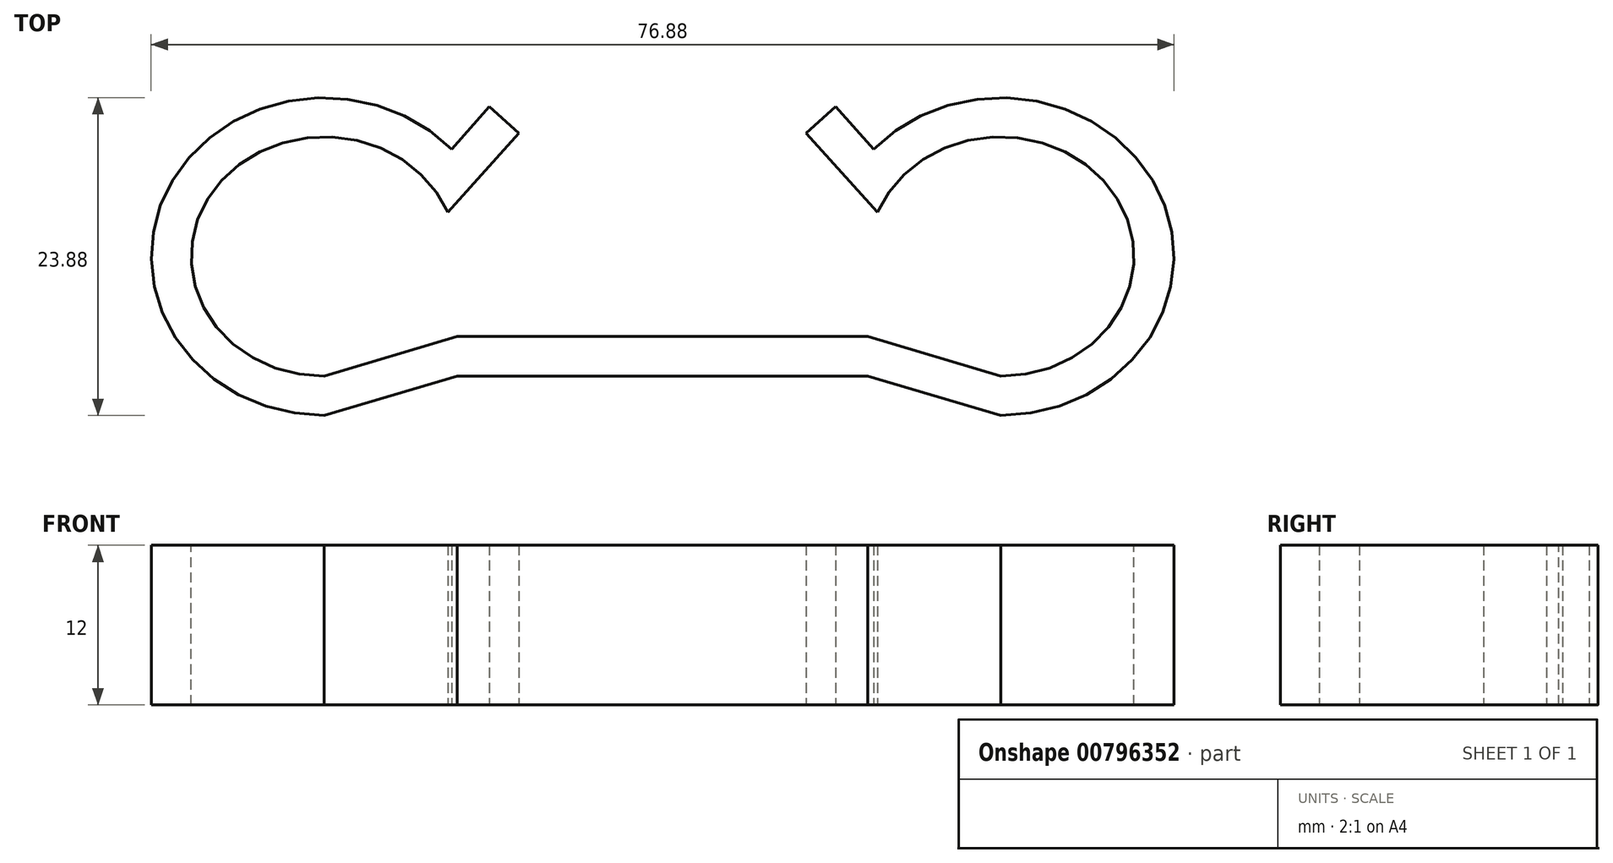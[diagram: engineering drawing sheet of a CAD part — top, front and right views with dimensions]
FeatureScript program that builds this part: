
annotation { "Feature Type Name" : "Feature", "Feature Type Description" : "" }
export const myFeature = defineFeature(function(context is Context, id is Id, definition is map)
    precondition{}
    {
        {
            var Q0;
            Q0=qCreatedBy(makeId("Top.planeOp"),FACE);
            var sketch = newSketch(context, id + "F0", { "sketchPlane" : qUnion([Q0])});
            skLineSegment(sketch, "E0.MirrorCS", {"start": v(0, 0) * mm, "end": v(15.44, 0) * mm});
            skLineSegment(sketch, "E1", {"start": v(-25.44, 0) * mm, "end": v(-25.44, 9) * mm, "construction": true});
            skLineSegment(sketch, "E2", {"start": v(-25.44, 9) * mm, "end": v(-35.44, 9) * mm, "construction": true});
            skLineSegment(sketch, "E3.MirrorCS", {"start": v(-25.44, 9) * mm, "end": v(-15.44, 9) * mm, "construction": true});
            skLineSegment(sketch, "E4.MirrorCS", {"start": v(-25.44, 18) * mm, "end": v(-25.44, 9) * mm, "construction": true});
            skEllipticalArc(sketch, "E5", {});
            skLineSegment(sketch, "E6", {"start": v(-15.44, 9) * mm, "end": v(-15.44, 3) * mm, "construction": true});
            skLineSegment(sketch, "E7", {"start": v(-15.44, 9) * mm, "end": v(-16.15, 12.33) * mm, "construction": true});
            skLineSegment(sketch, "E8", {"start": v(-16.15, 12.33) * mm, "end": v(-4.43, 12.33) * mm, "construction": true});
            skLineSegment(sketch, "E9", {"start": v(-16.15, 12.33) * mm, "end": v(-16.15, 23.8) * mm, "construction": true});
            skLineSegment(sketch, "E10", {"start": v(-16.15, 12.33) * mm, "end": v(-14.01, 14.7) * mm});
            skLineSegment(sketch, "E11", {"start": v(0, 0) * mm, "end": v(0, -2.94) * mm, "construction": true});
            skLineSegment(sketch, "E12", {"start": v(25.44, 0) * mm, "end": v(25.44, -2.94) * mm, "construction": true});
            skLineSegment(sketch, "E13.MirrorCS", {"start": v(-25.44, 0) * mm, "end": v(-25.44, -2.94) * mm, "construction": true});
            skLineSegment(sketch, "E14", {"start": v(-25.44, 18) * mm, "end": v(-25.44, 21) * mm, "construction": true});
            skPoint(sketch, "E15.MirrorCS.end.orphan", {"position": v(10.8, 18.28) * mm});
            skPoint(sketch, "E15.MirrorCS.start.orphan", {"position": v(16.15, 12.33) * mm});
            skPoint(sketch, "E16.MirrorCS.start.orphan", {"position": v(25.44, 0) * mm});
            skLineSegment(sketch, "E17", {"start": v(-35.44, 9) * mm, "end": v(-38.44, 9) * mm, "construction": true});
            skEllipticalArc(sketch, "E18", {});
            skLineSegment(sketch, "E19", {"start": v(-14.01, 14.7) * mm, "end": v(-15.86, 17.07) * mm, "construction": true});
            skLineSegment(sketch, "E20", {"start": v(-25.44, 18) * mm, "end": v(-15.86, 18) * mm, "construction": true});
            skLineSegment(sketch, "E21", {"start": v(-10.8, 18.28) * mm, "end": v(-13.03, 20.28) * mm});
            skLineSegment(sketch, "E22", {"start": v(-15.86, 17.07) * mm, "end": v(-13.03, 20.28) * mm});
            skEllipticalArc(sketch, "E23.MirrorCS", {});
            skEllipticalArc(sketch, "E24.MirrorCS", {});
            skPoint(sketch, "E25.MirrorCS.end.orphan", {"position": v(13.03, 20.28) * mm});
            skPoint(sketch, "E25.MirrorCS.start.orphan", {"position": v(15.86, 17.07) * mm});
            skLineSegment(sketch, "E26", {"start": v(-16.15, 12.33) * mm, "end": v(-10.8, 18.28) * mm});
            skLineSegment(sketch, "E27.MirrorCS", {"start": v(16.15, 12.33) * mm, "end": v(10.8, 18.28) * mm});
            skLineSegment(sketch, "E28.MirrorCS", {"start": v(10.8, 18.28) * mm, "end": v(13.03, 20.28) * mm});
            skLineSegment(sketch, "E29.MirrorCS", {"start": v(15.86, 17.07) * mm, "end": v(13.03, 20.28) * mm});
            skLineSegment(sketch, "E30", {"start": v(-15.44, 0) * mm, "end": v(-15.44, 3) * mm, "construction": true});
            skLineSegment(sketch, "E31", {"start": v(-25.44, 0) * mm, "end": v(-25.44, 3) * mm});
            skLineSegment(sketch, "E32", {"start": v(-25.44, 3) * mm, "end": v(-15.44, 3) * mm, "construction": true});
            skLineSegment(sketch, "E33", {"start": v(-25.44, 0) * mm, "end": v(-15.44, 3) * mm});
            skLineSegment(sketch, "E34", {"start": v(-25.44, -2.94) * mm, "end": v(-15.44, 0) * mm});
            skLineSegment(sketch, "E35", {"start": v(-15.44, 3) * mm, "end": v(0, 3) * mm});
            skLineSegment(sketch, "E36", {"start": v(-15.44, 0) * mm, "end": v(0, 0) * mm});
            skLineSegment(sketch, "E37.MirrorCS", {"start": v(25.44, 0) * mm, "end": v(15.44, 3) * mm});
            skLineSegment(sketch, "E38.MirrorCS", {"start": v(25.44, -2.94) * mm, "end": v(15.44, 0) * mm});
            skLineSegment(sketch, "E39.MirrorCS", {"start": v(15.44, 0) * mm, "end": v(15.44, 3) * mm, "construction": true});
            skLineSegment(sketch, "E40.MirrorCS", {"start": v(15.44, 3) * mm, "end": v(0, 3) * mm});
            const initialGuessF0  = {"E5": [-0.025436057219802476, 0.009, -1, 0, 0.01, 0.009, 3.5204317523090656, 1.5707963267948968], "E18": [-0.025436057219802476, 0.009, -1, 0, 0.013, 0.011935281219028263, 3.8837625004247056, 1.5707963267948968], "E23.MirrorCS": [0.025436057219802476, 0.009, 1, 0, 0.01, 0.009, 4.71238898038469, 2.762753554870521], "E23.MirrorCS": [0.025436057219802476, 0.009, 1, 0, 0.01, 0.009, 4.71238898038469, 2.762753554870521], "E24.MirrorCS": [0.025436057219802476, 0.009, 1, 0, 0.013, 0.011935281219028263, 4.71238898038469, 2.399422806754879]};
            skSetInitialGuess(sketch, initialGuessF0);
            skSolve(sketch);
        }
        {
            var Q0;
            Q0=makeQuery(id+"F0.imprint","IMPRINT",FACE,{"disambiguationData":[TD([[makeQuery(id+"F0.imprint","IMPRINT",EDGE,{"derivedFrom":sQuery(id+"F0.wireOp",EDGE,"E0.MirrorCS")}),1.0]])]});
            extrude(context, id + "F1", {"entities" : qUnion([Q0]), "depth" : 12 * mm, "offsetDistance" : 25 * mm});
        }
    });
